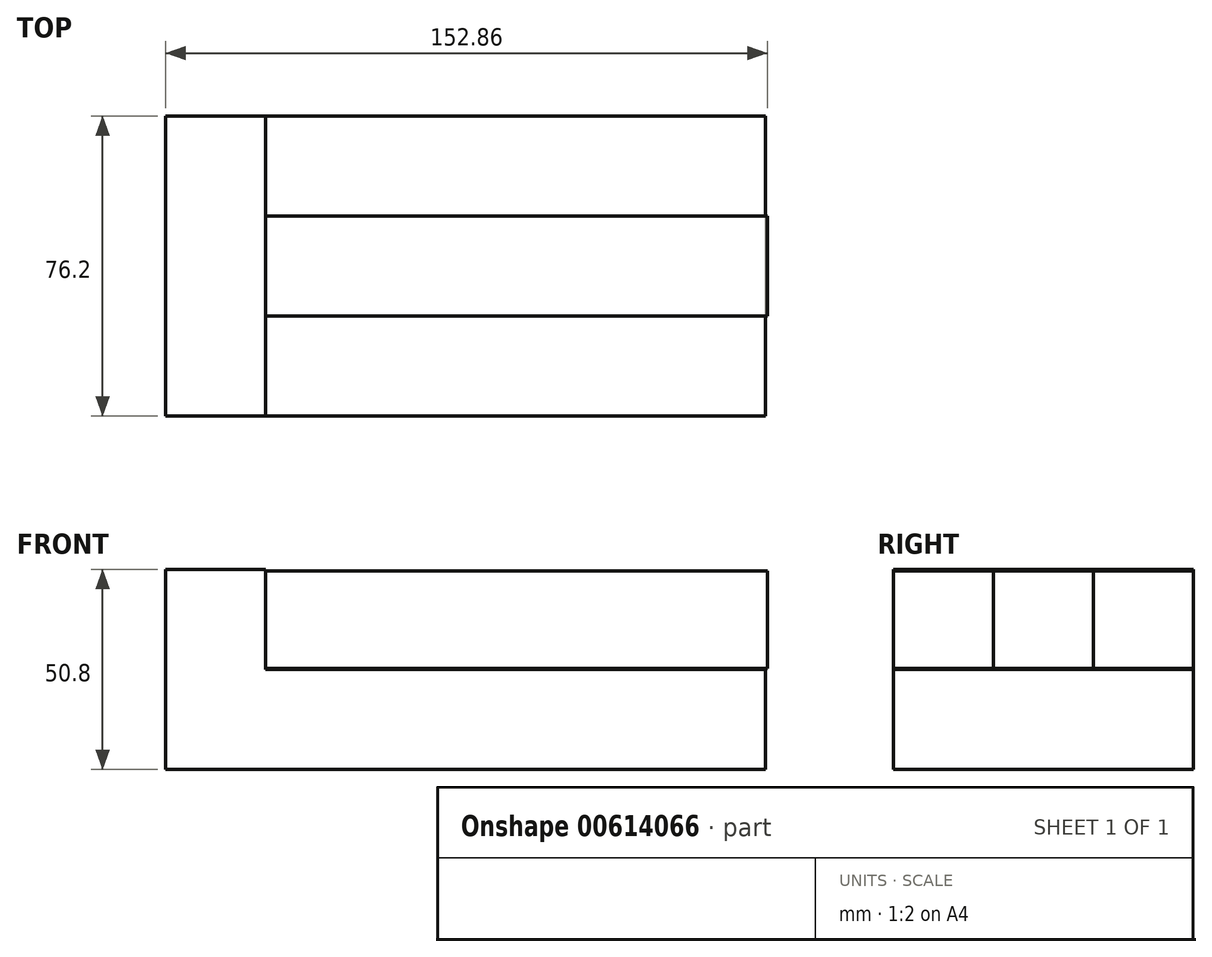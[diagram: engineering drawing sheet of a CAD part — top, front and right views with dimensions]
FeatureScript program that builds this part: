
annotation { "Feature Type Name" : "Feature", "Feature Type Description" : "" }
export const myFeature = defineFeature(function(context is Context, id is Id, definition is map)
    precondition{}
    {
        {
            var Q0;
            Q0=qCreatedBy(makeId("Front.planeOp"),FACE);
            var sketch = newSketch(context, id + "F0", { "sketchPlane" : qUnion([Q0])});
            skLineSegment(sketch, "E0.bottom", {"start": v(-53.5, 0.37) * mm, "end": v(98.9, 0.37) * mm});
            skLineSegment(sketch, "E0.top", {"start": v(-53.5, -50.43) * mm, "end": v(98.9, -50.43) * mm});
            skLineSegment(sketch, "E0.left", {"start": v(-53.5, 0.37) * mm, "end": v(-53.5, -50.43) * mm});
            skLineSegment(sketch, "E0.right", {"start": v(98.9, 0.37) * mm, "end": v(98.9, -50.43) * mm});
            skSolve(sketch);
        }
        {
            var Q0;
            Q0=makeQuery(id+"F0.imprint","IMPRINT",FACE,{"disambiguationData":[TD([[makeQuery(id+"F0.imprint","IMPRINT",EDGE,{"derivedFrom":sQuery(id+"F0.wireOp",EDGE,"E0.bottom")}),-1.0]])]});
            extrude(context, id + "F1", {"entities" : qUnion([Q0]), "oppositeDirection" : true, "depth" : 76.2 * mm, "offsetDistance" : 25.4 * mm});
        }
        {
            var Q0;
            Q0=makeQuery(id+"F1.opExtrude","SWEPT_FACE",FACE,{"disambiguationData":[OSD([sQuery(id+"F0.wireOp",EDGE,"E0.bottom")])]});
            var sketch = newSketch(context, id + "F2", { "sketchPlane" : qUnion([Q0])});
            skLineSegment(sketch, "E1.bottom", {"start": v(-28.1, 76.2) * mm, "end": v(98.9, 76.2) * mm});
            skLineSegment(sketch, "E1.top", {"start": v(-28.1, 0) * mm, "end": v(98.9, 0) * mm});
            skLineSegment(sketch, "E1.left", {"start": v(-28.1, 76.2) * mm, "end": v(-28.1, 0) * mm});
            skLineSegment(sketch, "E1.right", {"start": v(98.9, 76.2) * mm, "end": v(98.9, 0) * mm});
            skSolve(sketch);
        }
        {
            var Q0;
            Q0=makeQuery(id+"F2.imprint","IMPRINT",FACE,{"disambiguationData":[TD([[makeQuery(id+"F2.imprint","IMPRINT",EDGE,{"derivedFrom":sQuery(id+"F2.wireOp",EDGE,"E1.bottom")}),-1.0]])]});
            extrude(context, id + "F3", {"entities" : qUnion([Q0]), "operationType" : NewBodyOperationType.REMOVE, "oppositeDirection" : true, "depth" : 25.4 * mm, "offsetDistance" : 25.4 * mm});
        }
        {
            var Q0;
            Q0=qCreatedBy(makeId("Front.planeOp"),FACE);
            var sketch = newSketch(context, id + "F4", { "sketchPlane" : qUnion([Q0])});
            skLineSegment(sketch, "E2.bottom", {"start": v(-28.15, 0) * mm, "end": v(99.36, 0) * mm});
            skLineSegment(sketch, "E2.top", {"start": v(-28.15, -24.77) * mm, "end": v(99.36, -24.77) * mm});
            skLineSegment(sketch, "E2.left", {"start": v(-28.15, 0) * mm, "end": v(-28.15, -24.77) * mm});
            skLineSegment(sketch, "E2.right", {"start": v(99.36, 0) * mm, "end": v(99.36, -24.77) * mm});
            skSolve(sketch);
        }
        {
            var Q0;
            Q0=makeQuery(id+"F4.imprint","IMPRINT",FACE,{"disambiguationData":[TD([[makeQuery(id+"F4.imprint","IMPRINT",EDGE,{"derivedFrom":sQuery(id+"F4.wireOp",EDGE,"E2.bottom")}),-1.0]])]});
            extrude(context, id + "F5", {"entities" : qUnion([Q0]), "oppositeDirection" : true, "depth" : 76.2 * mm, "offsetDistance" : 25.4 * mm});
        }
        {
            var Q0;
            Q0=makeQuery(id+"F5.opExtrude","CAP_FACE",FACE,{"disambiguationData":[OSD([sQuery(id+"F4.wireOp",EDGE,"E2.bottom"),sQuery(id+"F4.wireOp",EDGE,"E2.top"),sQuery(id+"F4.wireOp",EDGE,"E2.left"),sQuery(id+"F4.wireOp",EDGE,"E2.right")])],"isStart":true});
            extrude(context, id + "F6", {"entities" : qUnion([Q0]), "operationType" : NewBodyOperationType.REMOVE, "oppositeDirection" : true, "depth" : 25.4 * mm, "offsetDistance" : 25.4 * mm});
        }
        {
            var Q0;
            Q0=makeQuery(id+"F5.opExtrude","CAP_FACE",FACE,{"disambiguationData":[OSD([sQuery(id+"F4.wireOp",EDGE,"E2.bottom"),sQuery(id+"F4.wireOp",EDGE,"E2.top"),sQuery(id+"F4.wireOp",EDGE,"E2.left"),sQuery(id+"F4.wireOp",EDGE,"E2.right")])],"isStart":false});
            extrude(context, id + "F7", {"entities" : qUnion([Q0]), "operationType" : NewBodyOperationType.REMOVE, "oppositeDirection" : true, "depth" : 25.4 * mm, "offsetDistance" : 25.4 * mm});
        }
        {
            var Q0;
            Q0=makeQuery(id+"F6.boolean.opBoolean","COPY",FACE,{"derivedFrom":makeQuery(id+"F6.opExtrude","CAP_FACE",FACE,{"disambiguationData":[OSD([sQuery(id+"F4.wireOp",EDGE,"E2.bottom"),sQuery(id+"F4.wireOp",EDGE,"E2.top"),sQuery(id+"F4.wireOp",EDGE,"E2.left"),sQuery(id+"F4.wireOp",EDGE,"E2.right")])],"isStart":false})});
            var sketch = newSketch(context, id + "F8", { "sketchPlane" : qUnion([Q0])});
            skLineSegment(sketch, "E3", {"start": v(-28.15, 0) * mm, "end": v(99.36, -24.77) * mm});
            skLineSegment(sketch, "E4", {"start": v(99.36, -24.77) * mm, "end": v(99.36, 0) * mm});
            skLineSegment(sketch, "E5", {"start": v(99.36, 0) * mm, "end": v(-28.15, 0) * mm});
            skSolve(sketch);
        }
        {
            var Q0;
            Q0=makeQuery(id+"F8.imprint","IMPRINT",FACE,{"disambiguationData":[TD([[makeQuery(id+"F8.imprint","IMPRINT",EDGE,{"derivedFrom":sQuery(id+"F8.wireOp",EDGE,"E3")}),1.0]])]});
            extrude(context, id + "F9", {"entities" : qUnion([Q0]), "operationType" : NewBodyOperationType.REMOVE, "oppositeDirection" : true, "depth" : 25.4 * mm, "offsetDistance" : 25.4 * mm});
        }
    });
